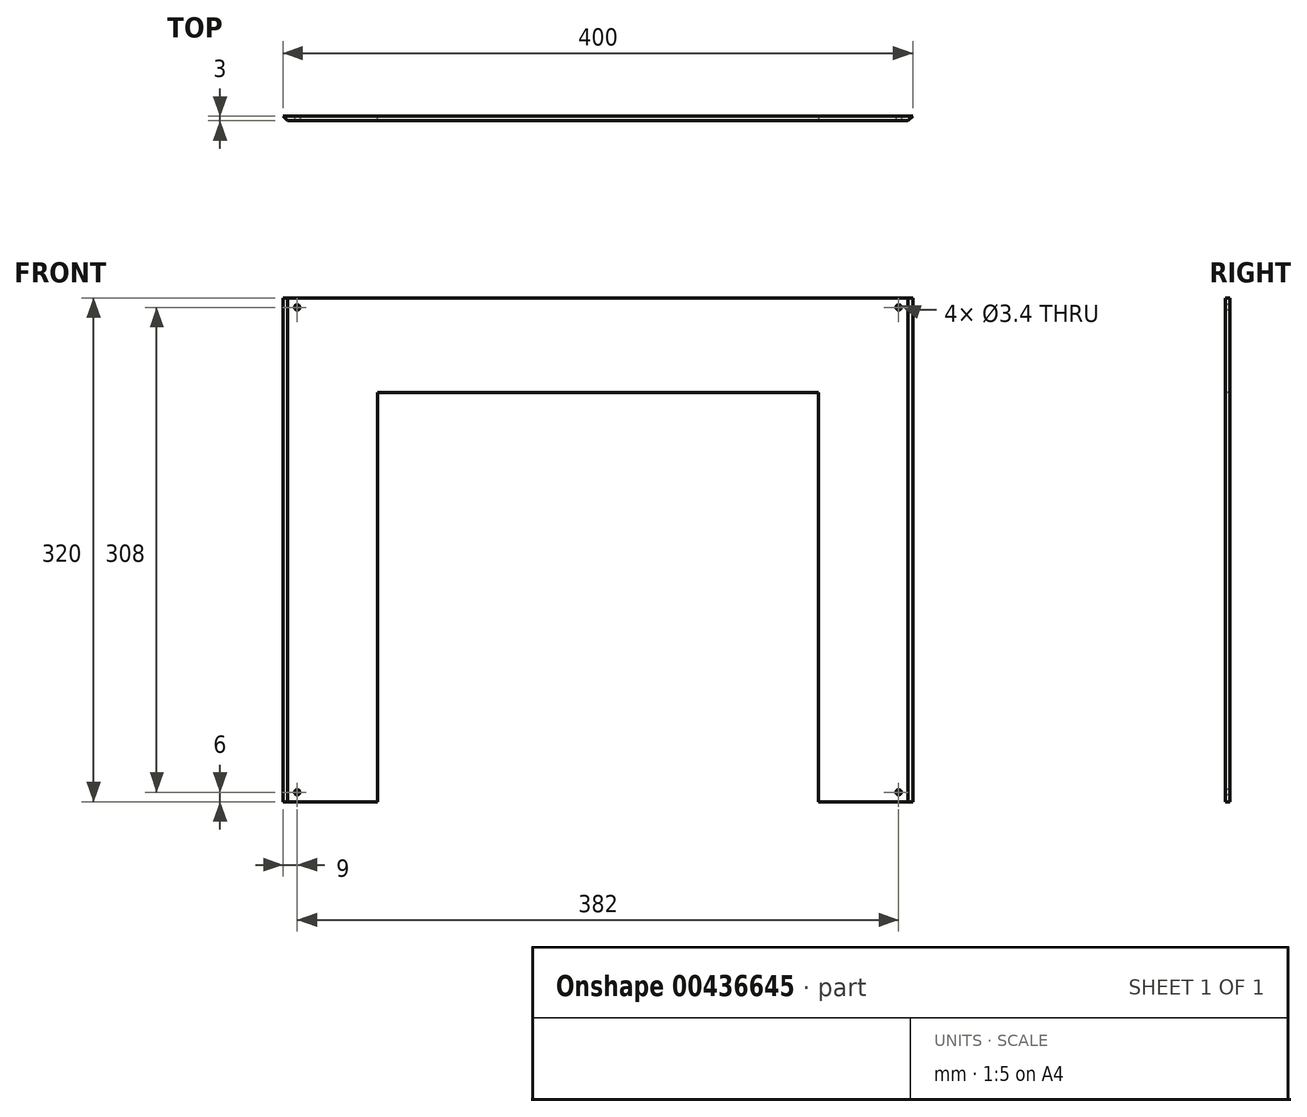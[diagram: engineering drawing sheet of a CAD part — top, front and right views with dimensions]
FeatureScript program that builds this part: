
annotation { "Feature Type Name" : "Feature", "Feature Type Description" : "" }
export const myFeature = defineFeature(function(context is Context, id is Id, definition is map)
    precondition{}
    {
        {
            var Q0;
            Q0=qCreatedBy(makeId("Top.planeOp"),FACE);
            var sketch = newSketch(context, id + "F0", { "sketchPlane" : qUnion([Q0])});
            skLineSegment(sketch, "E0", {"start": v(0, 0) * mm, "end": v(0, 1.5) * mm, "construction": true});
            skLineSegment(sketch, "E1", {"start": v(0, 0) * mm, "end": v(0, -1.5) * mm, "construction": true});
            skLineSegment(sketch, "E2", {"start": v(0, 1.5) * mm, "end": v(-200, 1.5) * mm});
            skLineSegment(sketch, "E3", {"start": v(0, 1.5) * mm, "end": v(200, 1.5) * mm});
            skLineSegment(sketch, "E4", {"start": v(0, -1.5) * mm, "end": v(-197, -1.5) * mm});
            skLineSegment(sketch, "E5", {"start": v(0, -1.5) * mm, "end": v(197, -1.5) * mm});
            skLineSegment(sketch, "E6", {"start": v(-197, -1.5) * mm, "end": v(-200, 1.5) * mm});
            skLineSegment(sketch, "E7", {"start": v(197, -1.5) * mm, "end": v(200, 1.5) * mm});
            skLineSegment(sketch, "E8", {"start": v(0, 0) * mm, "end": v(140, 0) * mm, "construction": true});
            skLineSegment(sketch, "E9", {"start": v(0, 0) * mm, "end": v(-140, 0) * mm, "construction": true});
            skLineSegment(sketch, "E10", {"start": v(140, 0) * mm, "end": v(140, 1.5) * mm});
            skLineSegment(sketch, "E11", {"start": v(140, 0) * mm, "end": v(140, -1.5) * mm});
            skLineSegment(sketch, "E12", {"start": v(-140, 0) * mm, "end": v(-140, 1.5) * mm});
            skLineSegment(sketch, "E13", {"start": v(-140, 0) * mm, "end": v(-140, -1.5) * mm});
            skSolve(sketch);
        }
        {
            var Q0;
            {var subQ8=sQuery(id+"F0.wireOp",EDGE,"E10");Q0=makeQuery(id+"F0.imprint","IMPRINT",FACE,{"disambiguationData":[TD([[makeQuery(id+"F0.imprint","IMPRINT",EDGE,{"derivedFrom":subQ8}),1.0]])]});}
            extrude(context, id + "F1", {"entities" : qUnion([Q0]), "oppositeDirection" : true, "depth" : 60 * mm});
        }
        {
            var Q0;
            {var subQ1=sQuery(id+"F0.wireOp",EDGE,"E6");Q0=makeQuery(id+"F0.imprint","IMPRINT",FACE,{"disambiguationData":[TD([[makeQuery(id+"F0.imprint","IMPRINT",EDGE,{"derivedFrom":subQ1}),-1.0]])]});}
            var Q1;
            {var subQ1=sQuery(id+"F0.wireOp",EDGE,"E7");Q1=makeQuery(id+"F0.imprint","IMPRINT",FACE,{"disambiguationData":[TD([[makeQuery(id+"F0.imprint","IMPRINT",EDGE,{"derivedFrom":subQ1}),1.0]])]});}
            extrude(context, id + "F2", {"entities" : qUnion([Q0, Q1]), "operationType" : NewBodyOperationType.ADD, "oppositeDirection" : true, "depth" : 320 * mm});
        }
        {
            var Q0;
            {var subQ0=sQuery(id+"F0.wireOp",EDGE,"E5");var subQ1=sQuery(id+"F0.wireOp",EDGE,"E4");Q0=makeQuery(id+"F2.boolean.opBoolean","MERGE",FACE,{"derivedFrom":[makeQuery(id+"F1.opExtrude","SWEPT_FACE",FACE,{"disambiguationData":[OSD([subQ1,subQ0])]}),makeQuery(id+"F2.opExtrude","SWEPT_FACE",FACE,{"disambiguationData":[OSD([subQ1])]}),makeQuery(id+"F2.opExtrude","SWEPT_FACE",FACE,{"disambiguationData":[OSD([subQ0])]})]});}
            var sketch = newSketch(context, id + "F3", { "sketchPlane" : qUnion([Q0])});
            skLineSegment(sketch, "E14", {"start": v(0, 0) * mm, "end": v(-191, 0) * mm, "construction": true});
            skLineSegment(sketch, "E15", {"start": v(-191, 0) * mm, "end": v(-191, -6) * mm, "construction": true});
            skCircle(sketch, "E16", {"center": v(-191, -6) * mm, "radius": 1.7 * mm});
            skLineSegment(sketch, "E17", {"start": v(-191, -6) * mm, "end": v(-191, -314) * mm, "construction": true});
            skCircle(sketch, "E18", {"center": v(-191, -314) * mm, "radius": 1.7 * mm});
            skLineSegment(sketch, "E19", {"start": v(0, 0) * mm, "end": v(191, 0) * mm, "construction": true});
            skLineSegment(sketch, "E20", {"start": v(191, 0) * mm, "end": v(191, -6) * mm, "construction": true});
            skLineSegment(sketch, "E21", {"start": v(191, -6) * mm, "end": v(191, -314) * mm, "construction": true});
            skCircle(sketch, "E22", {"center": v(191, -6) * mm, "radius": 1.7 * mm});
            skCircle(sketch, "E23", {"center": v(191, -314) * mm, "radius": 1.7 * mm});
            skSolve(sketch);
        }
        {
            var Q0;
            Q0=makeQuery(id+"F3.imprint","IMPRINT",FACE,{"disambiguationData":[TD([[makeQuery(id+"F3.imprint","IMPRINT",EDGE,{"derivedFrom":sQuery(id+"F3.wireOp",EDGE,"E22")}),1.0]])]});
            var Q1;
            Q1=makeQuery(id+"F3.imprint","IMPRINT",FACE,{"disambiguationData":[TD([[makeQuery(id+"F3.imprint","IMPRINT",EDGE,{"derivedFrom":sQuery(id+"F3.wireOp",EDGE,"E23")}),1.0]])]});
            var Q2;
            Q2=makeQuery(id+"F3.imprint","IMPRINT",FACE,{"disambiguationData":[TD([[makeQuery(id+"F3.imprint","IMPRINT",EDGE,{"derivedFrom":sQuery(id+"F3.wireOp",EDGE,"E18")}),1.0]])]});
            var Q3;
            Q3=makeQuery(id+"F3.imprint","IMPRINT",FACE,{"disambiguationData":[TD([[makeQuery(id+"F3.imprint","IMPRINT",EDGE,{"derivedFrom":sQuery(id+"F3.wireOp",EDGE,"E16")}),1.0]])]});
            extrude(context, id + "F4", {"entities" : qUnion([Q0, Q1, Q2, Q3]), "operationType" : NewBodyOperationType.REMOVE, "oppositeDirection" : true, "depth" : 3 * mm});
        }
    });
